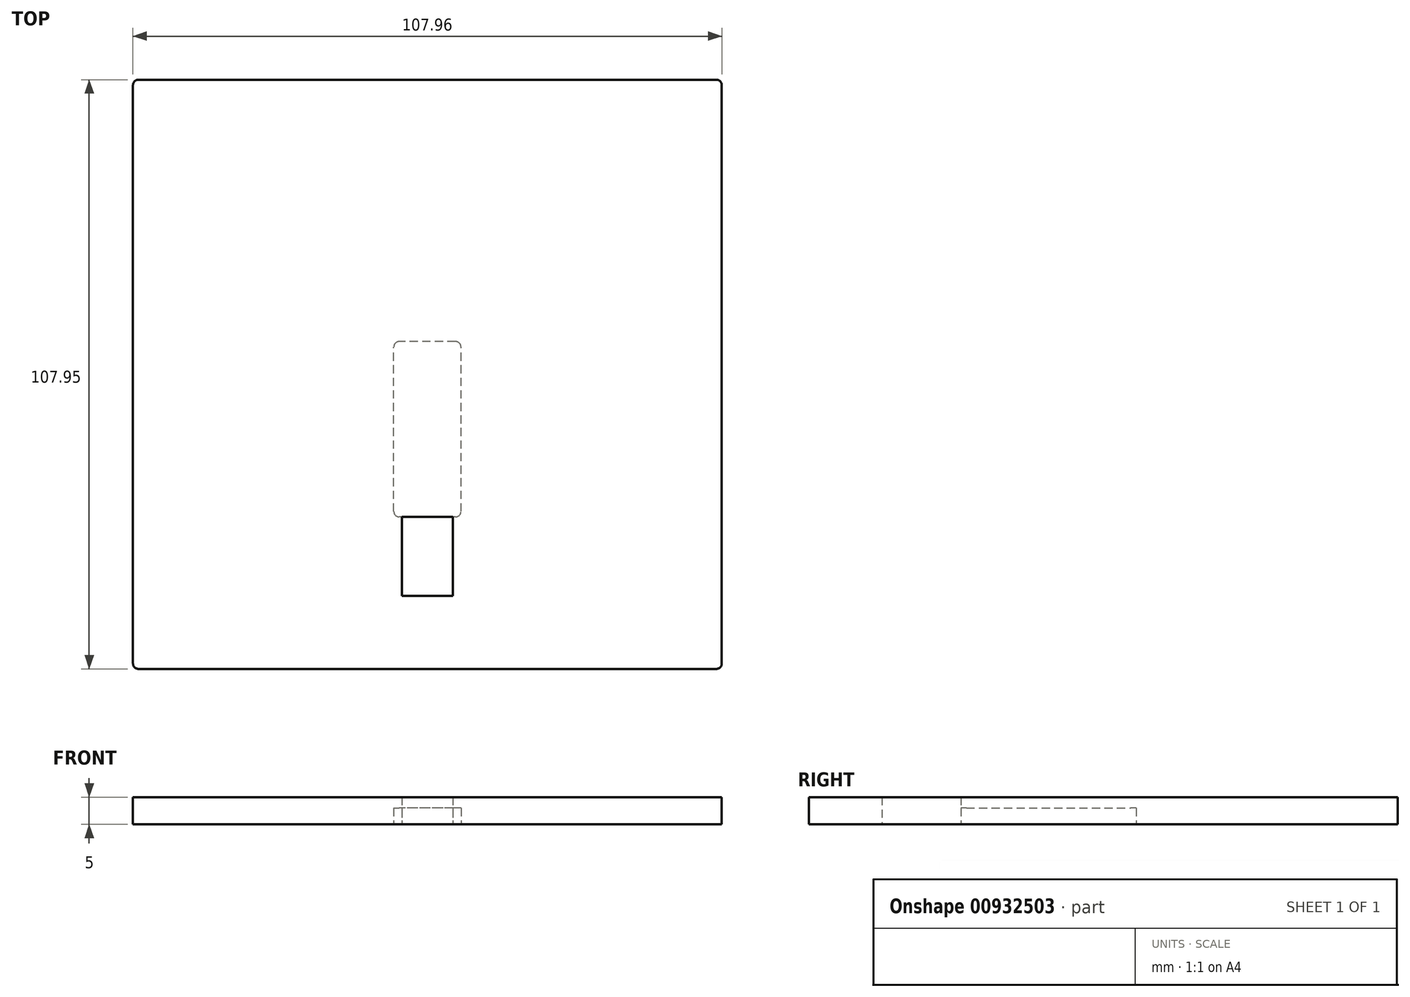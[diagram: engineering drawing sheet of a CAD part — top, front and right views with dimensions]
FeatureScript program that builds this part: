
annotation { "Feature Type Name" : "Feature", "Feature Type Description" : "" }
export const myFeature = defineFeature(function(context is Context, id is Id, definition is map)
    precondition{}
    {
        {
            var Q0;
            Q0=qCreatedBy(makeId("Top.planeOp"),FACE);
            var sketch = newSketch(context, id + "F0", { "sketchPlane" : qUnion([Q0])});
            skLineSegment(sketch, "E0.bottom", {"start": v(4.66, 40.63) * mm, "end": v(-4.66, 40.63) * mm});
            skLineSegment(sketch, "E0.top", {"start": v(4.66, -4.5) * mm, "end": v(-4.66, -4.5) * mm});
            skLineSegment(sketch, "E0.left", {"start": v(4.66, 40.63) * mm, "end": v(4.66, -4.5) * mm});
            skLineSegment(sketch, "E0.right", {"start": v(-4.66, 40.63) * mm, "end": v(-4.66, -4.5) * mm});
            skPoint(sketch, "E0.middle", {"position": v(0, 18.07) * mm});
            skLineSegment(sketch, "E1", {"start": v(0, 40.63) * mm, "end": v(0, -4.5) * mm, "construction": true});
            skLineSegment(sketch, "E2", {"start": v(4.66, 18.07) * mm, "end": v(-4.66, 18.07) * mm, "construction": true});
            skCircle(sketch, "E3", {"center": v(0, 36.13) * mm, "radius": 1.5 * mm});
            skCircle(sketch, "E4", {"center": v(0, 29.13) * mm, "radius": 1.5 * mm});
            skCircle(sketch, "E5.MirrorC", {"center": v(0, 7) * mm, "radius": 1.5 * mm});
            skCircle(sketch, "E6.MirrorC", {"center": v(0, 0) * mm, "radius": 1.5 * mm});
            skLineSegment(sketch, "E7.bottom", {"start": v(53.97, -17.85) * mm, "end": v(-53.98, -17.85) * mm});
            skLineSegment(sketch, "E7.top", {"start": v(53.98, 90.1) * mm, "end": v(-53.98, 90.1) * mm});
            skLineSegment(sketch, "E7.left", {"start": v(53.97, -17.85) * mm, "end": v(53.98, 90.1) * mm});
            skLineSegment(sketch, "E7.right", {"start": v(-53.98, -17.85) * mm, "end": v(-53.98, 90.1) * mm});
            skLineSegment(sketch, "E8", {"start": v(-4.66, 10) * mm, "end": v(4.66, 10) * mm});
            skLineSegment(sketch, "E9", {"start": v(0, -6) * mm, "end": v(6.16, -6) * mm});
            skLineSegment(sketch, "E10", {"start": v(6.16, -6) * mm, "end": v(6.16, 42.13) * mm});
            skLineSegment(sketch, "E11", {"start": v(6.16, 42.13) * mm, "end": v(0, 42.13) * mm});
            skLineSegment(sketch, "E12", {"start": v(4.66, 10) * mm, "end": v(6.16, 10) * mm});
            skLineSegment(sketch, "E13.MirrorCS", {"start": v(0, -6) * mm, "end": v(-6.16, -6) * mm});
            skLineSegment(sketch, "E14.MirrorCS", {"start": v(-6.16, 42.13) * mm, "end": v(0, 42.13) * mm});
            skLineSegment(sketch, "E15.MirrorCS", {"start": v(-6.16, -6) * mm, "end": v(-6.16, 42.13) * mm});
            skLineSegment(sketch, "E16", {"start": v(-4.66, 10) * mm, "end": v(-6.16, 10) * mm});
            skSolve(sketch);
        }
        {
            var Q0;
            Q0=makeQuery(id+"F0.imprint","IMPRINT",FACE,{"disambiguationData":[TD([[makeQuery(id+"F0.imprint","IMPRINT",EDGE,{"derivedFrom":sQuery(id+"F0.wireOp",EDGE,"E7.bottom")}),-1.0]])]});
            var Q1;
            {var subQ2=sQuery(id+"F0.wireOp",EDGE,"E0.top");Q1=makeQuery(id+"F0.imprint","IMPRINT",FACE,{"disambiguationData":[TD([[makeQuery(id+"F0.imprint","IMPRINT",EDGE,{"derivedFrom":subQ2}),1.0]])]});}
            var Q2;
            {var subQ1=sQuery(id+"F0.wireOp",EDGE,"E0.top");Q2=makeQuery(id+"F0.imprint","IMPRINT",FACE,{"disambiguationData":[TD([[makeQuery(id+"F0.imprint","IMPRINT",EDGE,{"derivedFrom":subQ1}),-1.0]])]});}
            var Q3;
            {var subQ1=sQuery(id+"F0.wireOp",EDGE,"E0.bottom");Q3=makeQuery(id+"F0.imprint","IMPRINT",FACE,{"disambiguationData":[TD([[makeQuery(id+"F0.imprint","IMPRINT",EDGE,{"derivedFrom":subQ1}),1.0]])]});}
            var Q4;
            {var subQ1=sQuery(id+"F0.wireOp",EDGE,"E0.bottom");Q4=makeQuery(id+"F0.imprint","IMPRINT",FACE,{"disambiguationData":[TD([[makeQuery(id+"F0.imprint","IMPRINT",EDGE,{"derivedFrom":subQ1}),-1.0]])]});}
            var Q5;
            Q5=makeQuery(id+"F0.imprint","IMPRINT",FACE,{"disambiguationData":[TD([[makeQuery(id+"F0.imprint","IMPRINT",EDGE,{"derivedFrom":sQuery(id+"F0.wireOp",EDGE,"E4")}),1.0]])]});
            var Q6;
            Q6=makeQuery(id+"F0.imprint","IMPRINT",FACE,{"disambiguationData":[TD([[makeQuery(id+"F0.imprint","IMPRINT",EDGE,{"derivedFrom":sQuery(id+"F0.wireOp",EDGE,"E3")}),1.0]])]});
            var Q7;
            Q7=makeQuery(id+"F0.imprint","IMPRINT",FACE,{"disambiguationData":[TD([[makeQuery(id+"F0.imprint","IMPRINT",EDGE,{"derivedFrom":sQuery(id+"F0.wireOp",EDGE,"E5.MirrorC")}),-1.0]])]});
            var Q8;
            Q8=makeQuery(id+"F0.imprint","IMPRINT",FACE,{"disambiguationData":[TD([[makeQuery(id+"F0.imprint","IMPRINT",EDGE,{"derivedFrom":sQuery(id+"F0.wireOp",EDGE,"E6.MirrorC")}),-1.0]])]});
            extrude(context, id + "F1", {"entities" : qUnion([Q0, Q1, Q2, Q3, Q4, Q5, Q6, Q7, Q8]), "depth" : 5 * mm, "offsetDistance" : 25 * mm});
        }
        {
            var Q0;
            {var subQ1=sQuery(id+"F0.wireOp",EDGE,"E0.bottom");Q0=makeQuery(id+"F0.imprint","IMPRINT",FACE,{"disambiguationData":[TD([[makeQuery(id+"F0.imprint","IMPRINT",EDGE,{"derivedFrom":subQ1}),-1.0]])]});}
            var Q1;
            {var subQ1=sQuery(id+"F0.wireOp",EDGE,"E0.bottom");Q1=makeQuery(id+"F0.imprint","IMPRINT",FACE,{"disambiguationData":[TD([[makeQuery(id+"F0.imprint","IMPRINT",EDGE,{"derivedFrom":subQ1}),1.0]])]});}
            var Q2;
            Q2=makeQuery(id+"F0.imprint","IMPRINT",FACE,{"disambiguationData":[TD([[makeQuery(id+"F0.imprint","IMPRINT",EDGE,{"derivedFrom":sQuery(id+"F0.wireOp",EDGE,"E4")}),1.0]])]});
            var Q3;
            Q3=makeQuery(id+"F0.imprint","IMPRINT",FACE,{"disambiguationData":[TD([[makeQuery(id+"F0.imprint","IMPRINT",EDGE,{"derivedFrom":sQuery(id+"F0.wireOp",EDGE,"E3")}),1.0]])]});
            extrude(context, id + "F2", {"entities" : qUnion([Q0, Q1, Q2, Q3]), "operationType" : NewBodyOperationType.REMOVE, "depth" : 3 * mm, "offsetDistance" : 25 * mm});
        }
        {
            var Q0;
            Q0=makeQuery(id+"F0.imprint","IMPRINT",FACE,{"disambiguationData":[TD([[makeQuery(id+"F0.imprint","IMPRINT",EDGE,{"derivedFrom":sQuery(id+"F0.wireOp",EDGE,"E6.MirrorC")}),-1.0]])]});
            var Q1;
            Q1=makeQuery(id+"F0.imprint","IMPRINT",FACE,{"disambiguationData":[TD([[makeQuery(id+"F0.imprint","IMPRINT",EDGE,{"derivedFrom":sQuery(id+"F0.wireOp",EDGE,"E5.MirrorC")}),-1.0]])]});
            extrude(context, id + "F3", {"entities" : qUnion([Q0, Q1]), "operationType" : NewBodyOperationType.REMOVE, "endBound" : BoundingType.UP_TO_NEXT, "depth" : 25 * mm, "offsetDistance" : 25 * mm});
        }
        {
            var Q0;
            Q0=makeQuery(id+"F2.boolean.opBoolean","COPY",EDGE,{"derivedFrom":makeQuery(id+"F2.opExtrude","SWEPT_EDGE",EDGE,{"disambiguationData":[OSD([sQuery(id+"F0.wireOp",EDGE,"E10"),sQuery(id+"F0.wireOp",EDGE,"E11")])]})});
            var Q1;
            Q1=makeQuery(id+"F2.boolean.opBoolean","COPY",EDGE,{"derivedFrom":makeQuery(id+"F2.opExtrude","SWEPT_EDGE",EDGE,{"disambiguationData":[OSD([sQuery(id+"F0.wireOp",EDGE,"E10"),sQuery(id+"F0.wireOp",EDGE,"E12")])]})});
            var Q2;
            Q2=makeQuery(id+"F1.opExtrude","SWEPT_EDGE",EDGE,{"disambiguationData":[OSD([sQuery(id+"F0.wireOp",EDGE,"E7.top"),sQuery(id+"F0.wireOp",EDGE,"E7.right")])]});
            var Q3;
            Q3=makeQuery(id+"F1.opExtrude","SWEPT_EDGE",EDGE,{"disambiguationData":[OSD([sQuery(id+"F0.wireOp",EDGE,"E7.top"),sQuery(id+"F0.wireOp",EDGE,"E7.left")])]});
            var Q4;
            Q4=makeQuery(id+"F1.opExtrude","SWEPT_EDGE",EDGE,{"disambiguationData":[OSD([sQuery(id+"F0.wireOp",EDGE,"E7.bottom"),sQuery(id+"F0.wireOp",EDGE,"E7.right")])]});
            var Q5;
            Q5=makeQuery(id+"F2.boolean.opBoolean","COPY",EDGE,{"derivedFrom":makeQuery(id+"F2.opExtrude","SWEPT_EDGE",EDGE,{"disambiguationData":[OSD([sQuery(id+"F0.wireOp",EDGE,"E14.MirrorCS"),sQuery(id+"F0.wireOp",EDGE,"E15.MirrorCS")])]})});
            var Q6;
            Q6=makeQuery(id+"F1.opExtrude","SWEPT_EDGE",EDGE,{"disambiguationData":[OSD([sQuery(id+"F0.wireOp",EDGE,"E7.bottom"),sQuery(id+"F0.wireOp",EDGE,"E7.left")])]});
            var Q7;
            Q7=makeQuery(id+"F2.boolean.opBoolean","COPY",EDGE,{"derivedFrom":makeQuery(id+"F2.opExtrude","SWEPT_EDGE",EDGE,{"disambiguationData":[OSD([sQuery(id+"F0.wireOp",EDGE,"E15.MirrorCS"),sQuery(id+"F0.wireOp",EDGE,"E16")])]})});
            var Q8;
            Q8=makeQuery(id+"F3.boolean.opBoolean","COPY",EDGE,{"derivedFrom":makeQuery(id+"F3.opExtrude","CAP_EDGE",EDGE,{"disambiguationData":[OSD([sQuery(id+"F0.wireOp",EDGE,"E5.MirrorC")])],"isStart":true})});
            var Q9;
            Q9=makeQuery(id+"F3.boolean.opBoolean","COPY",EDGE,{"derivedFrom":makeQuery(id+"F3.opExtrude","CAP_EDGE",EDGE,{"disambiguationData":[OSD([sQuery(id+"F0.wireOp",EDGE,"E6.MirrorC")])],"isStart":true})});
            var Q10;
            Q10=makeQuery(id+"F3.boolean.opBoolean","COPY",EDGE,{"derivedFrom":makeQuery(id+"F3.opExtrude","CAP_EDGE",EDGE,{"disambiguationData":[OSD([sQuery(id+"F0.wireOp",EDGE,"E5.MirrorC")])],"isStart":false})});
            var Q11;
            Q11=makeQuery(id+"F3.boolean.opBoolean","COPY",EDGE,{"derivedFrom":makeQuery(id+"F3.opExtrude","CAP_EDGE",EDGE,{"disambiguationData":[OSD([sQuery(id+"F0.wireOp",EDGE,"E6.MirrorC")])],"isStart":false})});
            fillet(context, id + "F4", {"entities" : qUnion([Q0, Q1, Q2, Q3, Q4, Q5, Q6, Q7, Q8, Q9, Q10, Q11]), "radius" : 1 * mm, "tangentPropagation" : true, "allowEdgeOverflow" : false});
        }
    });
